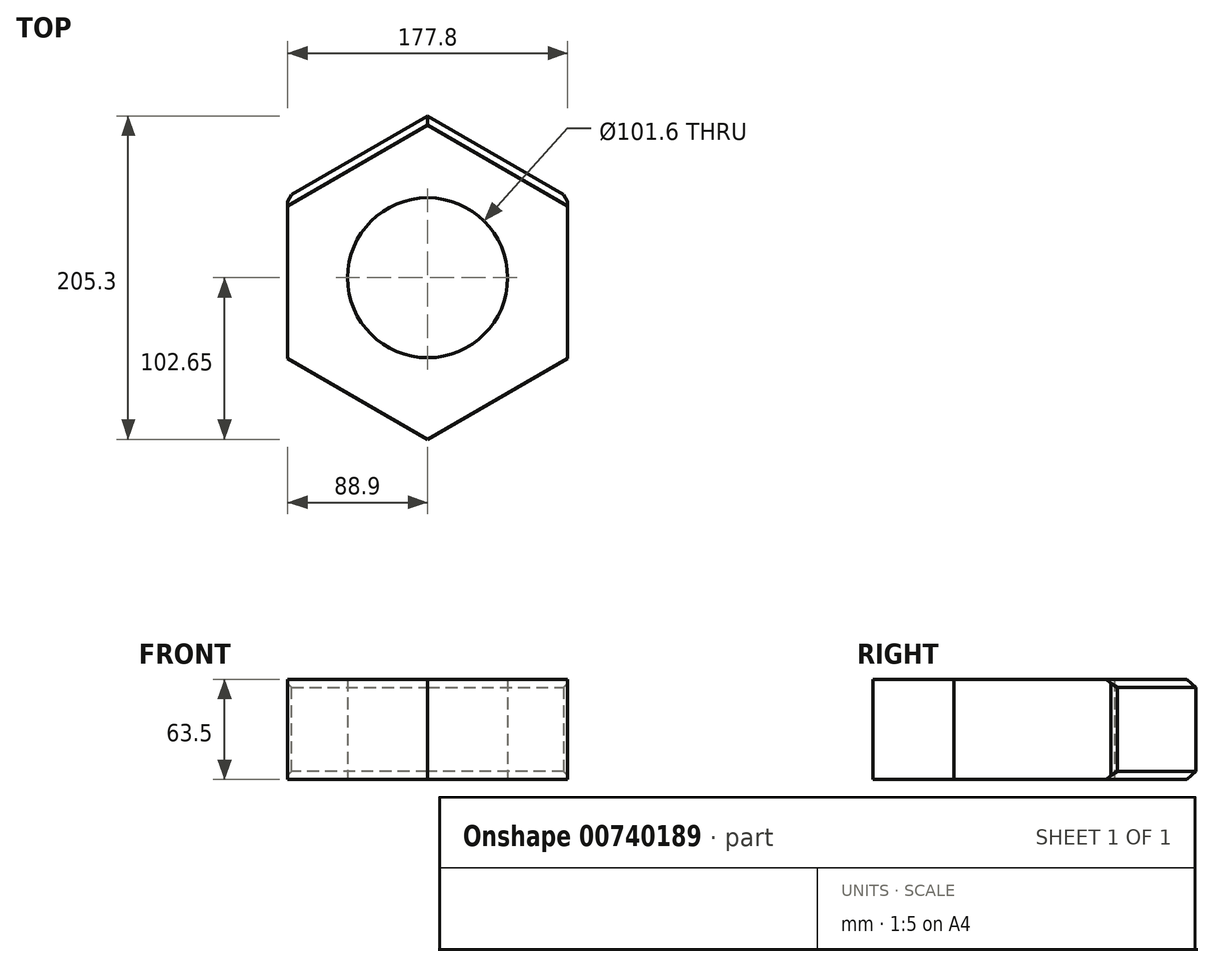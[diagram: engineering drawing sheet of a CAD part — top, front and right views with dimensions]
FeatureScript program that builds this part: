
annotation { "Feature Type Name" : "Feature", "Feature Type Description" : "" }
export const myFeature = defineFeature(function(context is Context, id is Id, definition is map)
    precondition{}
    {
        {
            var Q0;
            Q0=qCreatedBy(makeId("Top.planeOp"),FACE);
            var sketch = newSketch(context, id + "F0", { "sketchPlane" : qUnion([Q0])});
            skCircle(sketch, "E0.cCircle", {"center": v(0, 0) * mm, "radius": 88.9 * mm, "construction": true});
            skLineSegment(sketch, "E0.0", {"start": v(0, -102.65) * mm, "end": v(-88.9, -51.33) * mm});
            skLineSegment(sketch, "E0.1", {"start": v(-88.9, -51.33) * mm, "end": v(-88.9, 51.33) * mm});
            skLineSegment(sketch, "E0.2", {"start": v(-88.9, 51.33) * mm, "end": v(0, 102.65) * mm});
            skLineSegment(sketch, "E0.3", {"start": v(0, 102.65) * mm, "end": v(88.9, 51.33) * mm});
            skLineSegment(sketch, "E0.4", {"start": v(88.9, 51.33) * mm, "end": v(88.9, -51.33) * mm});
            skLineSegment(sketch, "E0.5", {"start": v(88.9, -51.33) * mm, "end": v(0, -102.65) * mm});
            skPoint(sketch, "E0.0.midPoint", {"position": v(-44.45, -76.99) * mm});
            skCircle(sketch, "E1", {"center": v(0, 0) * mm, "radius": 50.8 * mm});
            skSolve(sketch);
        }
        {
            var Q0;
            Q0 = qSketchRegion(id + "F0", true);
            extrude(context, id + "F1", {"entities" : qUnion([Q0]), "depth" : 63.5 * mm, "offsetDistance" : 25.4 * mm});
        }
        {
            var Q0;
            Q0=makeQuery(id+"F1.opExtrude","CAP_EDGE",EDGE,{"disambiguationData":[OSD([sQuery(id+"F0.wireOp",EDGE,"E0.3")])],"isStart":false});
            var Q1;
            Q1=makeQuery(id+"F1.opExtrude","CAP_EDGE",EDGE,{"disambiguationData":[OSD([sQuery(id+"F0.wireOp",EDGE,"E0.2")])],"isStart":false});
            var Q2;
            Q2=makeQuery(id+"F1.opExtrude","SWEPT_EDGE",EDGE,{"disambiguationData":[OSD([sQuery(id+"F0.wireOp",EDGE,"E0.1"),sQuery(id+"F0.wireOp",EDGE,"E0.2")])]});
            var Q3;
            Q3=makeQuery(id+"F1.opExtrude","CAP_EDGE",EDGE,{"disambiguationData":[OSD([sQuery(id+"F0.wireOp",EDGE,"E0.2")])],"isStart":true});
            var Q4;
            Q4=makeQuery(id+"F1.opExtrude","CAP_EDGE",EDGE,{"disambiguationData":[OSD([sQuery(id+"F0.wireOp",EDGE,"E0.3")])],"isStart":true});
            var Q5;
            Q5=makeQuery(id+"F1.opExtrude","SWEPT_EDGE",EDGE,{"disambiguationData":[OSD([sQuery(id+"F0.wireOp",EDGE,"E0.3"),sQuery(id+"F0.wireOp",EDGE,"E0.4")])]});
            chamfer(context, id + "F2", {"entities" : qUnion([Q0, Q1, Q2, Q3, Q4, Q5]), "width" : 5 * mm, "tangentPropagation" : true});
        }
    });
